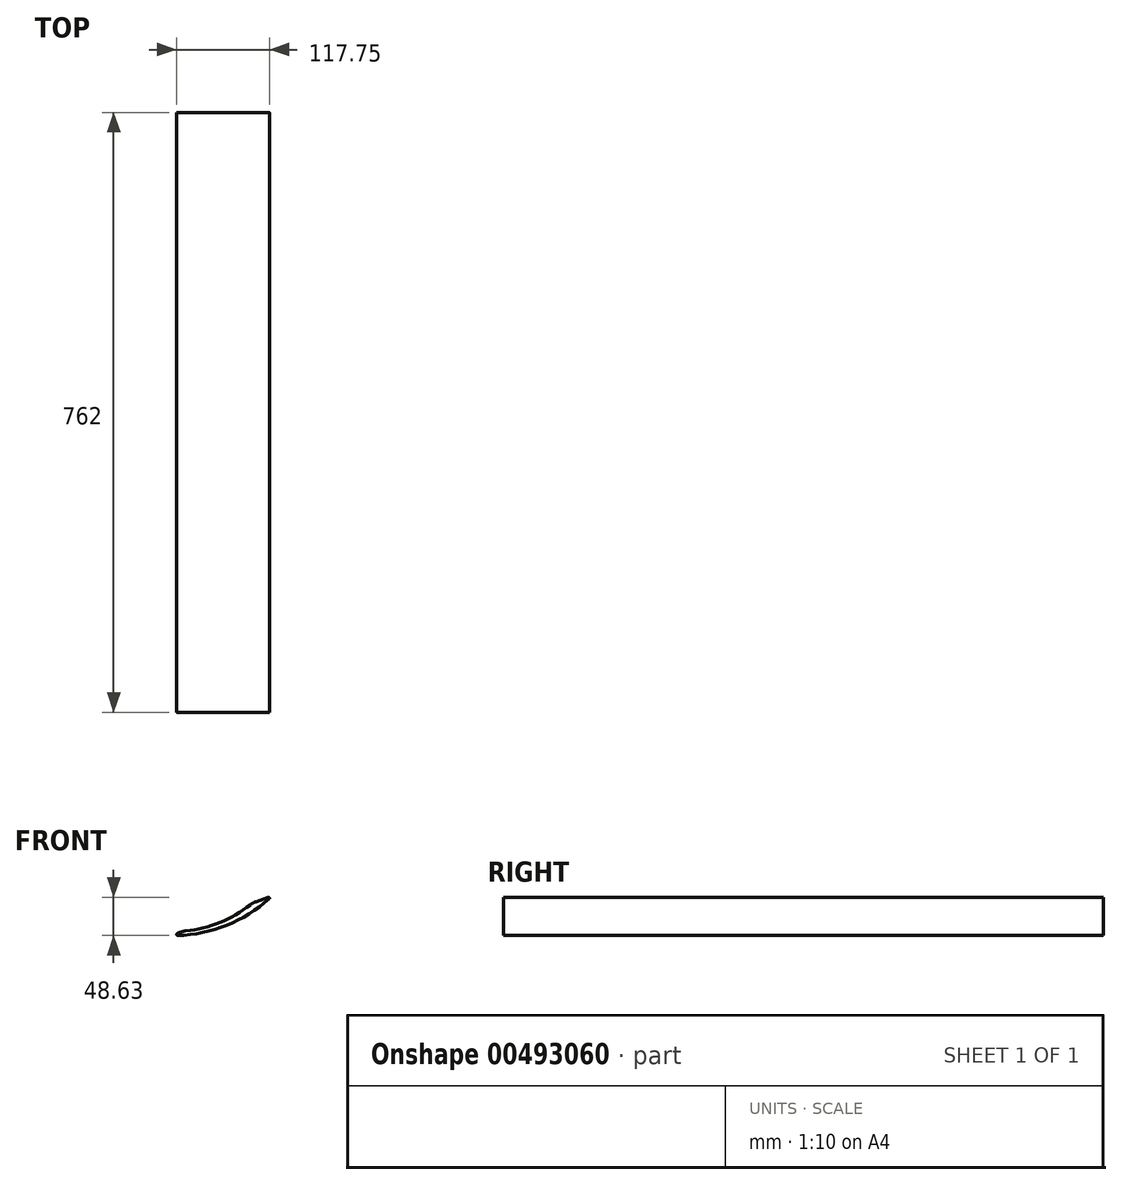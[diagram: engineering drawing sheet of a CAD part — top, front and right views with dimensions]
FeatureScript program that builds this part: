
annotation { "Feature Type Name" : "Feature", "Feature Type Description" : "" }
export const myFeature = defineFeature(function(context is Context, id is Id, definition is map)
    precondition{}
    {
        {
            var Q0;
            Q0=qCreatedBy(makeId("Front.planeOp"),FACE);
            var sketch = newSketch(context, id + "F0", { "sketchPlane" : qUnion([Q0])});
            skArc(sketch, "E0", {"start": v(-50.8, 5.59) * mm, "mid": v(-3.57, 16.77) * mm, "end": v(38.1, 41.64) * mm});
            skArc(sketch, "E1", {"start": v(-63.5, 0) * mm, "mid": v(4.9, 13.17) * mm, "end": v(63.5, 50.8) * mm});
            skPoint(sketch, "E2.visualSharp", {"position": v(48.26, 50.8) * mm});
            skLineSegment(sketch, "E3", {"start": v(63.5, 50.8) * mm, "end": v(38.1, 41.64) * mm});
            skLineSegment(sketch, "E4", {"start": v(-63.5, 0) * mm, "end": v(-50.8, 5.59) * mm});
            skPoint(sketch, "E5.orphan", {"position": v(63.5, 0) * mm});
            skPoint(sketch, "E6.trimOffspring.end.orphan", {"position": v(-50.8, 0) * mm});
            skSolve(sketch);
        }
        {
            var Q0;
            Q0=makeQuery(id+"F0.imprint","IMPRINT",FACE,{"disambiguationData":[TD([[makeQuery(id+"F0.imprint","IMPRINT",EDGE,{"derivedFrom":sQuery(id+"F0.wireOp",EDGE,"E0")}),-1.0]])]});
            extrude(context, id + "F1", {"entities" : qUnion([Q0]), "endBound" : BoundingType.SYMMETRIC, "oppositeDirection" : true, "depth" : 762 * mm});
        }
        {
            var Q0;
            Q0=makeQuery(id+"F1.opExtrude","SWEPT_EDGE",EDGE,{"disambiguationData":[OSD([sQuery(id+"F0.wireOp",EDGE,"E0"),sQuery(id+"F0.wireOp",EDGE,"E3")])]});
            var Q1;
            Q1=makeQuery(id+"F1.opExtrude","SWEPT_EDGE",EDGE,{"disambiguationData":[OSD([sQuery(id+"F0.wireOp",EDGE,"E0"),sQuery(id+"F0.wireOp",EDGE,"E4")])]});
            fillet(context, id + "F2", {"entities" : qUnion([Q0, Q1]), "radius" : 25.4 * mm, "tangentPropagation" : true, "allowEdgeOverflow" : false});
        }
        {
            var Q0;
            Q0=makeQuery(id+"F1.opExtrude","SWEPT_EDGE",EDGE,{"disambiguationData":[OSD([sQuery(id+"F0.wireOp",EDGE,"E1"),sQuery(id+"F0.wireOp",EDGE,"E4")])]});
            var Q1;
            Q1=makeQuery(id+"F1.opExtrude","SWEPT_EDGE",EDGE,{"disambiguationData":[OSD([sQuery(id+"F0.wireOp",EDGE,"E1"),sQuery(id+"F0.wireOp",EDGE,"E3")])]});
            fillet(context, id + "F3", {"entities" : qUnion([Q0, Q1]), "radius" : 1.27 * mm, "tangentPropagation" : true, "allowEdgeOverflow" : false});
        }
    });
